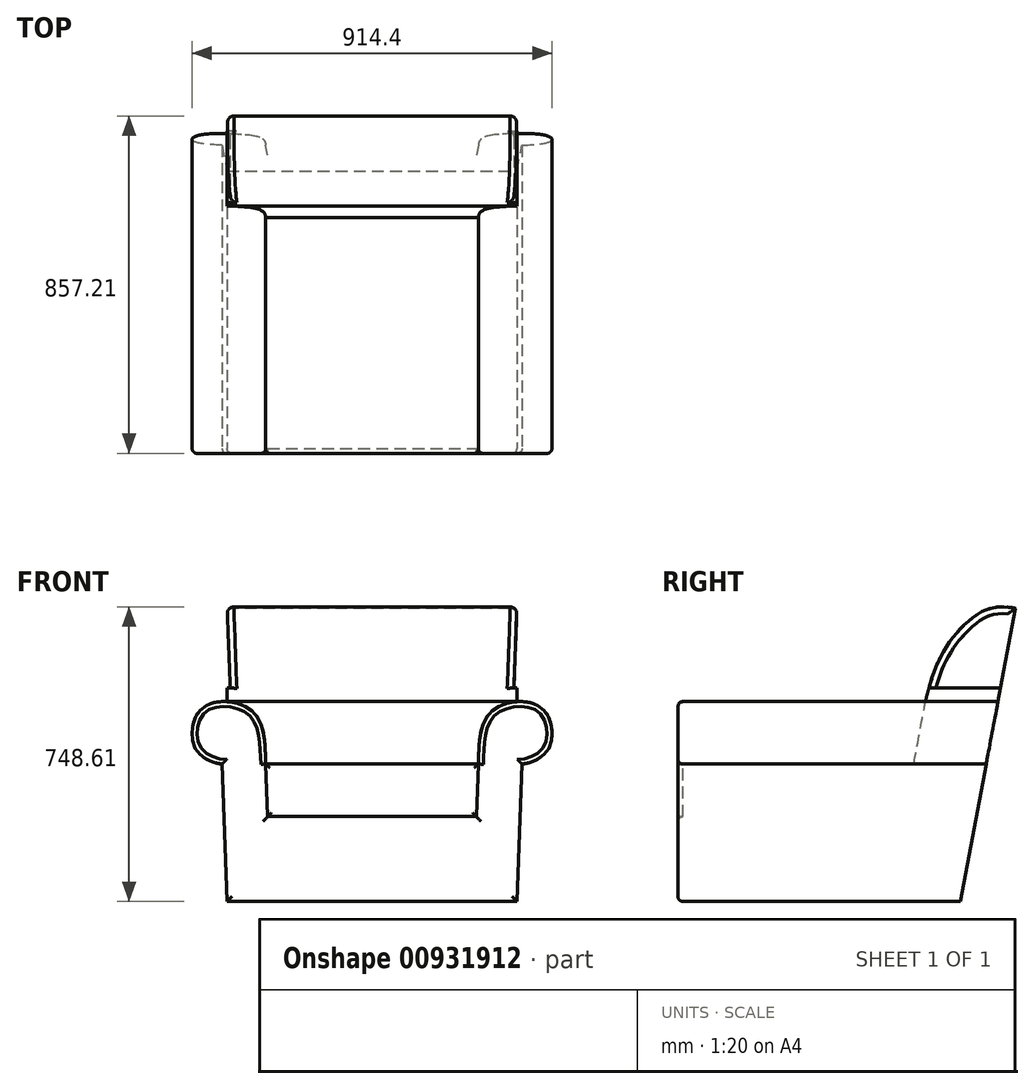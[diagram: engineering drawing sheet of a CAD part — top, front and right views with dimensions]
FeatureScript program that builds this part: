
annotation { "Feature Type Name" : "Feature", "Feature Type Description" : "" }
export const myFeature = defineFeature(function(context is Context, id is Id, definition is map)
    precondition{}
    {
        {
            var Q0;
            Q0=qCreatedBy(makeId("Front.planeOp"),FACE);
            var sketch = newSketch(context, id + "F0", { "sketchPlane" : qUnion([Q0])});
            skLineSegment(sketch, "E0", {"start": v(-368.3, -163.65) * mm, "end": v(368.3, -163.65) * mm});
            skLineSegment(sketch, "E1", {"start": v(-368.3, -163.65) * mm, "end": v(-381, 185.6) * mm});
            skLineSegment(sketch, "E2", {"start": v(381, 185.6) * mm, "end": v(368.3, -163.65) * mm});
            skLineSegment(sketch, "E3", {"start": v(-269.88, 185.6) * mm, "end": v(-265.03, 52.25) * mm});
            skLineSegment(sketch, "E4", {"start": v(-265.03, 52.25) * mm, "end": v(265.03, 52.25) * mm});
            skLineSegment(sketch, "E5", {"start": v(265.03, 52.25) * mm, "end": v(269.88, 185.6) * mm});
            skPoint(sketch, "E6", {"position": v(0, 52.25) * mm});
            skPoint(sketch, "E7", {"position": v(0, -163.65) * mm});
            skFitSpline(sketch, "E8", {"points": [v(269.88, 185.6) * mm, v(301.71, 317.05) * mm, v(428.37, 329.82) * mm, v(454.24, 239.6) * mm, v(420.79, 198.22) * mm, v(381, 185.6) * mm], "startDerivative": vector(24.12, 514.5) * mm, "endDerivative": vector(-224.77, -9.04) * mm});
            skLineSegment(sketch, "E9", {"start": v(234, 344.35) * mm, "end": v(456.81, 344.35) * mm, "construction": true});
            skLineSegment(sketch, "E10", {"start": v(457.2, 357.55) * mm, "end": v(457.2, 234.11) * mm, "construction": true});
            skLineSegment(sketch, "E11", {"start": v(0, 321) * mm, "end": v(0, 157.04) * mm, "construction": true});
            skFitSpline(sketch, "E12.MirrorCS", {"points": [v(-269.88, 185.6) * mm, v(-301.71, 317.05) * mm, v(-428.37, 329.82) * mm, v(-454.24, 239.6) * mm, v(-420.79, 198.22) * mm, v(-381, 185.6) * mm], "startDerivative": vector(-24.12, 514.5) * mm, "endDerivative": vector(224.77, -9.04) * mm});
            skSolve(sketch);
        }
        {
            var Q0;
            Q0=makeQuery(id+"F0.imprint","IMPRINT",FACE,{"disambiguationData":[TD([[makeQuery(id+"F0.imprint","IMPRINT",EDGE,{"derivedFrom":sQuery(id+"F0.wireOp",EDGE,"E0")}),1.0]])]});
            extrude(context, id + "F1", {"entities" : qUnion([Q0]), "oppositeDirection" : true, "depth" : 812.8 * mm});
        }
        {
            var Q0;
            Q0=qCreatedBy(makeId("Right.planeOp"),FACE);
            var sketch = newSketch(context, id + "F2", { "sketchPlane" : qUnion([Q0])});
            skLineSegment(sketch, "E13", {"start": v(812.8, 343.38) * mm, "end": v(717.55, -163.65) * mm});
            skLineSegment(sketch, "E14", {"start": v(717.55, -163.65) * mm, "end": v(717.55, -180.75) * mm});
            skLineSegment(sketch, "E15", {"start": v(717.55, -180.75) * mm, "end": v(830.02, -180.75) * mm});
            skLineSegment(sketch, "E16", {"start": v(830.02, -180.75) * mm, "end": v(830.02, 343.38) * mm});
            skLineSegment(sketch, "E17", {"start": v(830.02, 343.38) * mm, "end": v(812.8, 343.38) * mm});
            skSolve(sketch);
        }
        {
            var Q0;
            Q0=makeQuery(id+"F2.imprint","IMPRINT",FACE,{"disambiguationData":[TD([[makeQuery(id+"F2.imprint","IMPRINT",EDGE,{"derivedFrom":sQuery(id+"F2.wireOp",EDGE,"E13")}),1.0]])]});
            extrude(context, id + "F3", {"entities" : qUnion([Q0]), "operationType" : NewBodyOperationType.REMOVE, "oppositeDirection" : true, "depth" : 1219.2 * mm, "symmetric" : true});
        }
        {
            var Q0;
            Q0=qCreatedBy(makeId("Right.planeOp"),FACE);
            var sketch = newSketch(context, id + "F4", { "sketchPlane" : qUnion([Q0])});
            skPoint(sketch, "E18.0", {"position": v(758.1, 52.25) * mm});
            skLineSegment(sketch, "E19", {"start": v(758.1, 52.25) * mm, "end": v(857.2, 581.53) * mm});
            skLineSegment(sketch, "E20", {"start": v(0, 344.35) * mm, "end": v(812.8, 344.35) * mm, "construction": true});
            skLineSegment(sketch, "E21.0", {"start": v(758.1, 52.25) * mm, "end": v(0, 52.25) * mm, "construction": true});
            skLineSegment(sketch, "E22", {"start": v(84.79, 179.25) * mm, "end": v(861.12, 179.25) * mm, "construction": true});
            skFitSpline(sketch, "E23", {"points": [v(857.2, 581.53) * mm, v(767.16, 569.77) * mm, v(687.44, 491.95) * mm, v(628.65, 344.35) * mm], "startDerivative": vector(-409.99, 73.48) * mm, "endDerivative": vector(-132.5, -535.48) * mm});
            skLineSegment(sketch, "E24", {"start": v(628.65, 344.35) * mm, "end": v(573.96, 52.25) * mm});
            skLineSegment(sketch, "E25", {"start": v(573.96, 52.25) * mm, "end": v(758.1, 52.25) * mm});
            skSolve(sketch);
        }
        {
            var Q0;
            Q0=makeQuery(id+"F4.imprint","IMPRINT",FACE,{"disambiguationData":[TD([[makeQuery(id+"F4.imprint","IMPRINT",EDGE,{"derivedFrom":sQuery(id+"F4.wireOp",EDGE,"E19")}),1.0]])]});
            extrude(context, id + "F5", {"entities" : qUnion([Q0]), "operationType" : NewBodyOperationType.ADD, "depth" : 736.6 * mm, "symmetric" : true});
        }
        {
            var Q0;
            Q0=makeQuery(id+"F0.imprint","IMPRINT",FACE,{"disambiguationData":[TD([[makeQuery(id+"F0.imprint","IMPRINT",EDGE,{"derivedFrom":sQuery(id+"F0.wireOp",EDGE,"E0")}),1.0]])]});
            var sketch = newSketch(context, id + "F6", { "sketchPlane" : qUnion([Q0])});
            skFitSpline(sketch, "E26.0", {"points": [v(269.88, 185.6) * mm, v(271.9, 228.63) * mm, v(267.64, 341.13) * mm, v(450.12, 358.81) * mm, v(465.5, 235.12) * mm, v(424.97, 195.93) * mm, v(391.44, 186.02) * mm, v(381, 185.6) * mm]});
            skLineSegment(sketch, "E27", {"start": v(-368.3, 584.96) * mm, "end": v(368.3, 584.96) * mm, "construction": true});
            skLineSegment(sketch, "E28", {"start": v(368.3, 584.96) * mm, "end": v(368.3, 344.06) * mm});
            skLineSegment(sketch, "E29", {"start": v(368.3, 584.96) * mm, "end": v(358.78, 343.03) * mm});
            skLineSegment(sketch, "E30.0", {"start": v(0, 321) * mm, "end": v(0, 157.04) * mm, "construction": true});
            skLineSegment(sketch, "E31.MirrorCS", {"start": v(-368.3, 584.96) * mm, "end": v(-358.78, 343.03) * mm});
            skLineSegment(sketch, "E32.MirrorCS", {"start": v(-368.3, 584.96) * mm, "end": v(-368.3, 344.06) * mm});
            skFitSpline(sketch, "E33.MirrorCS", {"points": [v(-269.88, 185.6) * mm, v(-271.9, 228.63) * mm, v(-267.64, 341.13) * mm, v(-450.12, 358.81) * mm, v(-465.5, 235.12) * mm, v(-424.97, 195.93) * mm, v(-391.44, 186.02) * mm, v(-381, 185.6) * mm]});
            skSolve(sketch);
        }
        {
            var Q0;
            {var subQ0=sQuery(id+"F6.wireOp",EDGE,"E31.MirrorCS");Q0=makeQuery(id+"F6.imprint","IMPRINT",FACE,{"disambiguationData":[TD([[makeQuery(id+"F6.imprint","IMPRINT",EDGE,{"derivedFrom":subQ0}),-1.0]])]});}
            var Q1;
            {var subQ0=sQuery(id+"F6.wireOp",EDGE,"E28");Q1=makeQuery(id+"F6.imprint","IMPRINT",FACE,{"disambiguationData":[TD([[makeQuery(id+"F6.imprint","IMPRINT",EDGE,{"derivedFrom":subQ0}),-1.0]])]});}
            extrude(context, id + "F7", {"entities" : qUnion([Q0, Q1]), "operationType" : NewBodyOperationType.REMOVE, "endBound" : BoundingType.THROUGH_ALL, "oppositeDirection" : true, "depth" : 25.4 * mm});
        }
        {
            var Q0;
            Q0=makeQuery(id+"F1.opExtrude","CAP_FACE",FACE,{"disambiguationData":[OSD([sQuery(id+"F0.wireOp",EDGE,"E0"),sQuery(id+"F0.wireOp",EDGE,"E1"),sQuery(id+"F0.wireOp",EDGE,"E2"),sQuery(id+"F0.wireOp",EDGE,"E3"),sQuery(id+"F0.wireOp",EDGE,"E4"),sQuery(id+"F0.wireOp",EDGE,"E5"),sQuery(id+"F0.wireOp",EDGE,"E8"),sQuery(id+"F0.wireOp",EDGE,"E12.MirrorCS")])],"isStart":true});
            fillet(context, id + "F8", {"entities" : qUnion([Q0]), "radius" : 12.7 * mm, "tangentPropagation" : true, "allowEdgeOverflow" : false});
        }
        {
            var Q0;
            Q0=makeQuery(id+"F0.imprint","IMPRINT",FACE,{"disambiguationData":[TD([[makeQuery(id+"F0.imprint","IMPRINT",EDGE,{"derivedFrom":sQuery(id+"F0.wireOp",EDGE,"E0")}),1.0]])]});
            var sketch = newSketch(context, id + "F9", { "sketchPlane" : qUnion([Q0])});
            skLineSegment(sketch, "E34.0", {"start": v(-269.88, 185.6) * mm, "end": v(-265.03, 52.25) * mm});
            skLineSegment(sketch, "E35.0", {"start": v(-265.03, 52.25) * mm, "end": v(265.03, 52.25) * mm});
            skLineSegment(sketch, "E36.0", {"start": v(265.03, 52.25) * mm, "end": v(269.88, 185.6) * mm});
            skLineSegment(sketch, "E37", {"start": v(-269.88, 185.6) * mm, "end": v(269.88, 185.6) * mm});
            skSolve(sketch);
        }
        {
            var Q0;
            Q0=makeQuery(id+"F9.imprint","IMPRINT",FACE,{"disambiguationData":[TD([[makeQuery(id+"F9.imprint","IMPRINT",EDGE,{"derivedFrom":sQuery(id+"F9.wireOp",EDGE,"E34.0")}),1.0]])]});
            extrude(context, id + "F10", {"entities" : qUnion([Q0]), "operationType" : NewBodyOperationType.ADD, "oppositeDirection" : true, "depth" : 673.1 * mm});
        }
        {
            var Q0;
            Q0=makeQuery(id+"F10.opExtrude","CAP_FACE",FACE,{"disambiguationData":[OSD([sQuery(id+"F9.wireOp",EDGE,"E34.0"),sQuery(id+"F9.wireOp",EDGE,"E35.0"),sQuery(id+"F9.wireOp",EDGE,"E36.0"),sQuery(id+"F9.wireOp",EDGE,"E37")])],"isStart":true});
            fillet(context, id + "F11", {"entities" : qUnion([Q0]), "radius" : 8.9 * mm, "tangentPropagation" : true, "allowEdgeOverflow" : false});
        }
        {
            var Q0;
            Q0=makeQuery(id+"F7.boolean.opBoolean","INTERSECT",EDGE,{"derivedFrom":[makeQuery(id+"F5.opExtrude","SWEPT_FACE",FACE,{"disambiguationData":[OSD([sQuery(id+"F4.wireOp",EDGE,"E23")])]}),makeQuery(id+"F7.opExtrude","SWEPT_FACE",FACE,{"disambiguationData":[OSD([sQuery(id+"F6.wireOp",EDGE,"E29")])]})]});
            var Q1;
            Q1=makeQuery(id+"F7.boolean.opBoolean","INTERSECT",EDGE,{"derivedFrom":[makeQuery(id+"F5.opExtrude","SWEPT_FACE",FACE,{"disambiguationData":[OSD([sQuery(id+"F4.wireOp",EDGE,"E19")])]}),makeQuery(id+"F7.opExtrude","SWEPT_FACE",FACE,{"disambiguationData":[OSD([sQuery(id+"F6.wireOp",EDGE,"E29")])]})]});
            var Q2;
            Q2=makeQuery(id+"F7.boolean.opBoolean","INTERSECT",EDGE,{"derivedFrom":[makeQuery(id+"F5.opExtrude","SWEPT_FACE",FACE,{"disambiguationData":[OSD([sQuery(id+"F4.wireOp",EDGE,"E19")])]}),makeQuery(id+"F7.opExtrude","SWEPT_FACE",FACE,{"disambiguationData":[OSD([sQuery(id+"F6.wireOp",EDGE,"E31.MirrorCS")])]})]});
            var Q3;
            Q3=makeQuery(id+"F7.boolean.opBoolean","INTERSECT",EDGE,{"derivedFrom":[makeQuery(id+"F5.opExtrude","SWEPT_FACE",FACE,{"disambiguationData":[OSD([sQuery(id+"F4.wireOp",EDGE,"E23")])]}),makeQuery(id+"F7.opExtrude","SWEPT_FACE",FACE,{"disambiguationData":[OSD([sQuery(id+"F6.wireOp",EDGE,"E31.MirrorCS")])]})]});
            fillet(context, id + "F12", {"entities" : qUnion([Q0, Q1, Q2, Q3]), "radius" : 16.5 * mm, "tangentPropagation" : true, "allowEdgeOverflow" : false});
        }
    });
